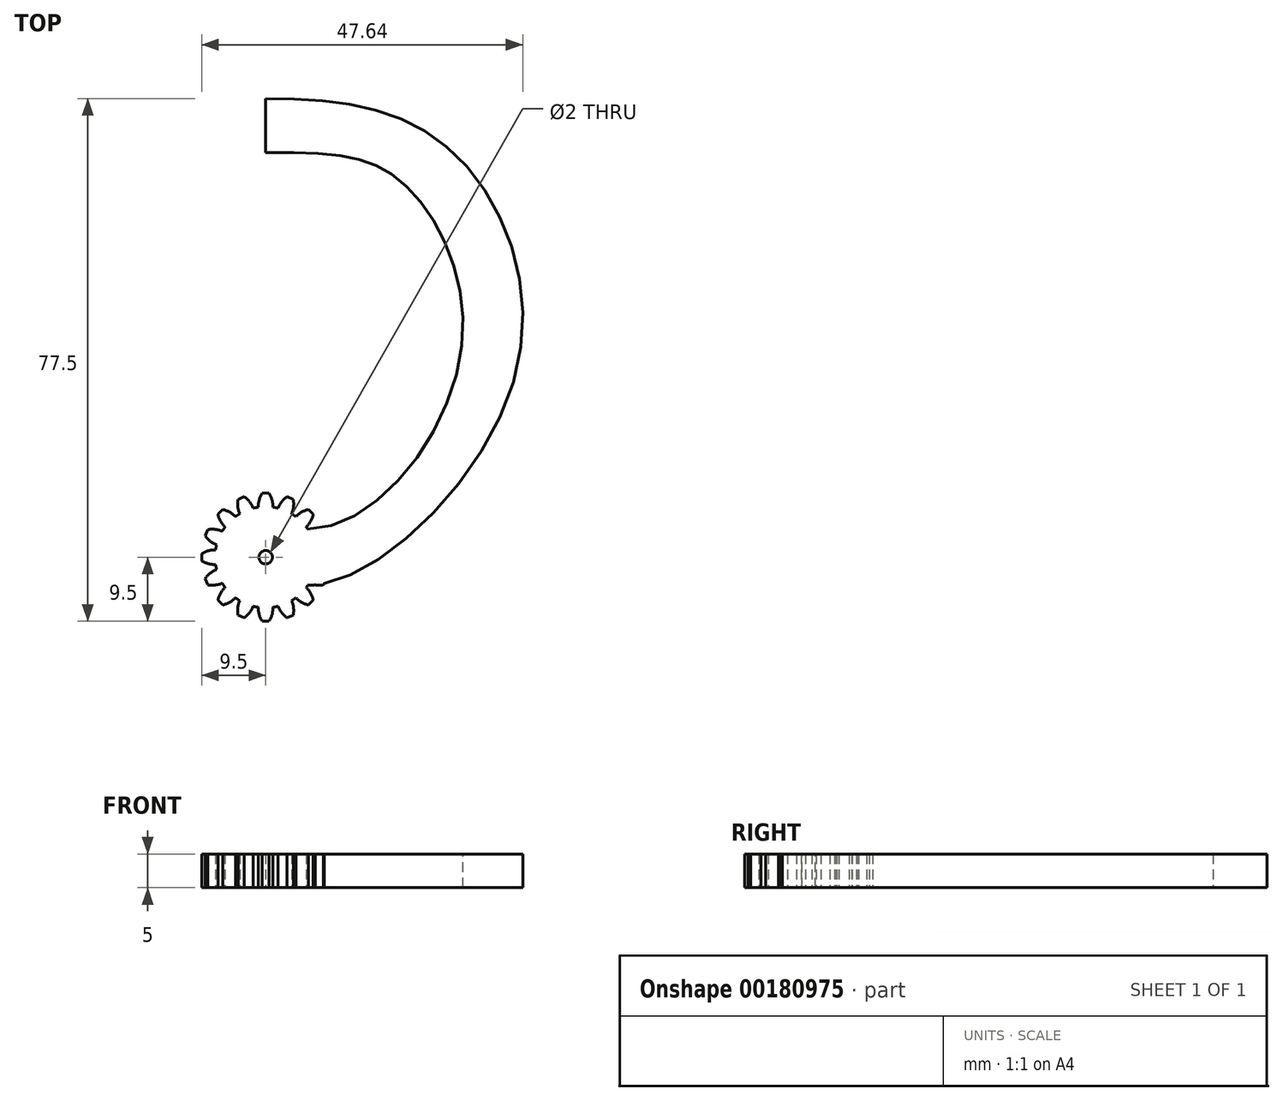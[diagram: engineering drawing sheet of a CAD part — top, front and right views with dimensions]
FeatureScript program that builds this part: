
annotation { "Feature Type Name" : "Feature", "Feature Type Description" : "" }
export const myFeature = defineFeature(function(context is Context, id is Id, definition is map)
    precondition{}
    {
        {
            var Q0;
            Q0=qCreatedBy(makeId("Top.planeOp"),FACE);
            var sketch = newSketch(context, id + "F0", { "sketchPlane" : qUnion([Q0])});
            skCircle(sketch, "E0", {"center": v(0, 0) * mm, "radius": 7.5 * mm});
            skLineSegment(sketch, "E1", {"start": v(0, 0) * mm, "end": v(0, 7.5) * mm, "construction": true});
            skLineSegment(sketch, "E2", {"start": v(0, 7.5) * mm, "end": v(0, 9.5) * mm});
            skLineSegment(sketch, "E3", {"start": v(0, 9.5) * mm, "end": v(-0.5, 9.5) * mm});
            skArc(sketch, "E4", {"start": v(-0.5, 9.5) * mm, "mid": v(-0.95, 8.5) * mm, "end": v(-1.09, 7.42) * mm});
            skLineSegment(sketch, "E5.MirrorCS", {"start": v(0, 9.5) * mm, "end": v(0.5, 9.5) * mm});
            skArc(sketch, "E6.MirrorCS", {"start": v(0.5, 9.5) * mm, "mid": v(0.95, 8.5) * mm, "end": v(1.09, 7.42) * mm});
            skArc(sketch, "E7.1.0", {"start": v(-4.1, 8.59) * mm, "mid": v(-4.13, 7.5) * mm, "end": v(-3.85, 6.44) * mm});
            skLineSegment(sketch, "E7.1.1", {"start": v(-3.64, 8.78) * mm, "end": v(-4.1, 8.59) * mm});
            skLineSegment(sketch, "E7.1.2", {"start": v(-3.64, 8.78) * mm, "end": v(-3.17, 8.97) * mm});
            skArc(sketch, "E7.1.3", {"start": v(-3.17, 8.97) * mm, "mid": v(-2.38, 8.22) * mm, "end": v(-1.83, 7.27) * mm});
            skArc(sketch, "E7.2.0", {"start": v(-7.07, 6.36) * mm, "mid": v(-6.69, 5.34) * mm, "end": v(-6.02, 4.48) * mm});
            skLineSegment(sketch, "E7.2.1", {"start": v(-6.72, 6.72) * mm, "end": v(-7.07, 6.36) * mm});
            skLineSegment(sketch, "E7.2.2", {"start": v(-6.72, 6.72) * mm, "end": v(-6.36, 7.07) * mm});
            skArc(sketch, "E7.2.3", {"start": v(-6.36, 7.07) * mm, "mid": v(-5.34, 6.69) * mm, "end": v(-4.48, 6.02) * mm});
            skArc(sketch, "E7.3.0", {"start": v(-8.97, 3.17) * mm, "mid": v(-8.22, 2.38) * mm, "end": v(-7.27, 1.83) * mm});
            skLineSegment(sketch, "E7.3.1", {"start": v(-8.78, 3.64) * mm, "end": v(-8.97, 3.17) * mm});
            skLineSegment(sketch, "E7.3.2", {"start": v(-8.78, 3.64) * mm, "end": v(-8.59, 4.1) * mm});
            skArc(sketch, "E7.3.3", {"start": v(-8.59, 4.1) * mm, "mid": v(-7.5, 4.13) * mm, "end": v(-6.44, 3.85) * mm});
            skArc(sketch, "E7.4.0", {"start": v(-9.5, -0.5) * mm, "mid": v(-8.5, -0.95) * mm, "end": v(-7.42, -1.09) * mm});
            skLineSegment(sketch, "E7.4.1", {"start": v(-9.5, 0) * mm, "end": v(-9.5, -0.5) * mm});
            skLineSegment(sketch, "E7.4.2", {"start": v(-9.5, 0) * mm, "end": v(-9.5, 0.5) * mm});
            skArc(sketch, "E7.4.3", {"start": v(-9.5, 0.5) * mm, "mid": v(-8.5, 0.95) * mm, "end": v(-7.42, 1.09) * mm});
            skArc(sketch, "E7.5.0", {"start": v(-8.59, -4.1) * mm, "mid": v(-7.5, -4.13) * mm, "end": v(-6.44, -3.85) * mm});
            skLineSegment(sketch, "E7.5.1", {"start": v(-8.78, -3.64) * mm, "end": v(-8.59, -4.1) * mm});
            skLineSegment(sketch, "E7.5.2", {"start": v(-8.78, -3.64) * mm, "end": v(-8.97, -3.17) * mm});
            skArc(sketch, "E7.5.3", {"start": v(-8.97, -3.17) * mm, "mid": v(-8.22, -2.38) * mm, "end": v(-7.27, -1.83) * mm});
            skArc(sketch, "E7.6.0", {"start": v(-6.36, -7.07) * mm, "mid": v(-5.34, -6.69) * mm, "end": v(-4.48, -6.02) * mm});
            skLineSegment(sketch, "E7.6.1", {"start": v(-6.72, -6.72) * mm, "end": v(-6.36, -7.07) * mm});
            skLineSegment(sketch, "E7.6.2", {"start": v(-6.72, -6.72) * mm, "end": v(-7.07, -6.36) * mm});
            skArc(sketch, "E7.6.3", {"start": v(-7.07, -6.36) * mm, "mid": v(-6.69, -5.34) * mm, "end": v(-6.02, -4.48) * mm});
            skArc(sketch, "E7.7.0", {"start": v(-3.17, -8.97) * mm, "mid": v(-2.38, -8.22) * mm, "end": v(-1.83, -7.27) * mm});
            skLineSegment(sketch, "E7.7.1", {"start": v(-3.64, -8.78) * mm, "end": v(-3.17, -8.97) * mm});
            skLineSegment(sketch, "E7.7.2", {"start": v(-3.64, -8.78) * mm, "end": v(-4.1, -8.59) * mm});
            skArc(sketch, "E7.7.3", {"start": v(-4.1, -8.59) * mm, "mid": v(-4.13, -7.5) * mm, "end": v(-3.85, -6.44) * mm});
            skArc(sketch, "E7.8.0", {"start": v(0.5, -9.5) * mm, "mid": v(0.95, -8.5) * mm, "end": v(1.09, -7.42) * mm});
            skLineSegment(sketch, "E7.8.1", {"start": v(0, -9.5) * mm, "end": v(0.5, -9.5) * mm});
            skLineSegment(sketch, "E7.8.2", {"start": v(0, -9.5) * mm, "end": v(-0.5, -9.5) * mm});
            skArc(sketch, "E7.8.3", {"start": v(-0.5, -9.5) * mm, "mid": v(-0.95, -8.5) * mm, "end": v(-1.09, -7.42) * mm});
            skArc(sketch, "E7.9.0", {"start": v(4.1, -8.59) * mm, "mid": v(4.13, -7.5) * mm, "end": v(3.85, -6.44) * mm});
            skLineSegment(sketch, "E7.9.1", {"start": v(3.64, -8.78) * mm, "end": v(4.1, -8.59) * mm});
            skLineSegment(sketch, "E7.9.2", {"start": v(3.64, -8.78) * mm, "end": v(3.17, -8.97) * mm});
            skArc(sketch, "E7.9.3", {"start": v(3.17, -8.97) * mm, "mid": v(2.38, -8.22) * mm, "end": v(1.83, -7.27) * mm});
            skArc(sketch, "E7.10.0", {"start": v(7.07, -6.36) * mm, "mid": v(6.69, -5.34) * mm, "end": v(6.02, -4.48) * mm});
            skLineSegment(sketch, "E7.10.1", {"start": v(6.72, -6.72) * mm, "end": v(7.07, -6.36) * mm});
            skLineSegment(sketch, "E7.10.2", {"start": v(6.72, -6.72) * mm, "end": v(6.36, -7.07) * mm});
            skArc(sketch, "E7.10.3", {"start": v(6.36, -7.07) * mm, "mid": v(5.34, -6.69) * mm, "end": v(4.48, -6.02) * mm});
            skArc(sketch, "E7.11.0", {"start": v(8.97, -3.17) * mm, "mid": v(8.22, -2.38) * mm, "end": v(7.27, -1.83) * mm});
            skLineSegment(sketch, "E7.11.1", {"start": v(8.78, -3.64) * mm, "end": v(8.97, -3.17) * mm});
            skLineSegment(sketch, "E7.11.2", {"start": v(8.78, -3.64) * mm, "end": v(8.59, -4.1) * mm});
            skArc(sketch, "E7.11.3", {"start": v(8.59, -4.1) * mm, "mid": v(7.5, -4.13) * mm, "end": v(6.44, -3.85) * mm});
            skArc(sketch, "E7.12.0", {"start": v(9.5, 0.5) * mm, "mid": v(8.5, 0.95) * mm, "end": v(7.42, 1.09) * mm});
            skLineSegment(sketch, "E7.12.1", {"start": v(9.5, 0) * mm, "end": v(9.5, 0.5) * mm});
            skLineSegment(sketch, "E7.12.2", {"start": v(9.5, 0) * mm, "end": v(9.5, -0.5) * mm});
            skArc(sketch, "E7.12.3", {"start": v(9.5, -0.5) * mm, "mid": v(8.5, -0.95) * mm, "end": v(7.42, -1.09) * mm});
            skArc(sketch, "E7.13.0", {"start": v(8.59, 4.1) * mm, "mid": v(7.5, 4.13) * mm, "end": v(6.44, 3.85) * mm});
            skLineSegment(sketch, "E7.13.1", {"start": v(8.78, 3.64) * mm, "end": v(8.59, 4.1) * mm});
            skLineSegment(sketch, "E7.13.2", {"start": v(8.78, 3.64) * mm, "end": v(8.97, 3.17) * mm});
            skArc(sketch, "E7.13.3", {"start": v(8.97, 3.17) * mm, "mid": v(8.22, 2.38) * mm, "end": v(7.27, 1.83) * mm});
            skArc(sketch, "E7.14.0", {"start": v(6.36, 7.07) * mm, "mid": v(5.34, 6.69) * mm, "end": v(4.48, 6.02) * mm});
            skLineSegment(sketch, "E7.14.1", {"start": v(6.72, 6.72) * mm, "end": v(6.36, 7.07) * mm});
            skLineSegment(sketch, "E7.14.2", {"start": v(6.72, 6.72) * mm, "end": v(7.07, 6.36) * mm});
            skArc(sketch, "E7.14.3", {"start": v(7.07, 6.36) * mm, "mid": v(6.69, 5.34) * mm, "end": v(6.02, 4.48) * mm});
            skArc(sketch, "E7.15.0", {"start": v(3.17, 8.97) * mm, "mid": v(2.38, 8.22) * mm, "end": v(1.83, 7.27) * mm});
            skLineSegment(sketch, "E7.15.1", {"start": v(3.64, 8.78) * mm, "end": v(3.17, 8.97) * mm});
            skLineSegment(sketch, "E7.15.2", {"start": v(3.64, 8.78) * mm, "end": v(4.1, 8.59) * mm});
            skArc(sketch, "E7.15.3", {"start": v(4.1, 8.59) * mm, "mid": v(4.13, 7.5) * mm, "end": v(3.85, 6.44) * mm});
            skSolve(sketch);
        }
        {
            var Q0;
            Q0=qSketchRegion(id+"F0",true);
            extrude(context, id + "F1", {"entities" : qUnion([Q0]), "depth" : 5 * mm});
        }
        {
            var Q0;
            Q0=makeQuery(id+"F1.opExtrude","CAP_FACE",FACE,{"disambiguationData":[OSD([sQuery(id+"F0.wireOp",EDGE,"E0"),sQuery(id+"F0.wireOp",EDGE,"E3"),sQuery(id+"F0.wireOp",EDGE,"E4"),sQuery(id+"F0.wireOp",EDGE,"E5.MirrorCS"),sQuery(id+"F0.wireOp",EDGE,"E6.MirrorCS"),sQuery(id+"F0.wireOp",EDGE,"E7.1.0"),sQuery(id+"F0.wireOp",EDGE,"E7.1.1"),sQuery(id+"F0.wireOp",EDGE,"E7.1.2"),sQuery(id+"F0.wireOp",EDGE,"E7.1.3"),sQuery(id+"F0.wireOp",EDGE,"E7.2.0"),sQuery(id+"F0.wireOp",EDGE,"E7.2.1"),sQuery(id+"F0.wireOp",EDGE,"E7.2.2"),sQuery(id+"F0.wireOp",EDGE,"E7.2.3"),sQuery(id+"F0.wireOp",EDGE,"E7.3.0"),sQuery(id+"F0.wireOp",EDGE,"E7.3.1"),sQuery(id+"F0.wireOp",EDGE,"E7.3.2"),sQuery(id+"F0.wireOp",EDGE,"E7.3.3"),sQuery(id+"F0.wireOp",EDGE,"E7.4.0"),sQuery(id+"F0.wireOp",EDGE,"E7.4.1"),sQuery(id+"F0.wireOp",EDGE,"E7.4.2"),sQuery(id+"F0.wireOp",EDGE,"E7.4.3"),sQuery(id+"F0.wireOp",EDGE,"E7.5.0"),sQuery(id+"F0.wireOp",EDGE,"E7.5.1"),sQuery(id+"F0.wireOp",EDGE,"E7.5.2"),sQuery(id+"F0.wireOp",EDGE,"E7.5.3"),sQuery(id+"F0.wireOp",EDGE,"E7.6.0"),sQuery(id+"F0.wireOp",EDGE,"E7.6.1"),sQuery(id+"F0.wireOp",EDGE,"E7.6.2"),sQuery(id+"F0.wireOp",EDGE,"E7.6.3"),sQuery(id+"F0.wireOp",EDGE,"E7.7.0"),sQuery(id+"F0.wireOp",EDGE,"E7.7.1"),sQuery(id+"F0.wireOp",EDGE,"E7.7.2"),sQuery(id+"F0.wireOp",EDGE,"E7.7.3"),sQuery(id+"F0.wireOp",EDGE,"E7.8.0"),sQuery(id+"F0.wireOp",EDGE,"E7.8.1"),sQuery(id+"F0.wireOp",EDGE,"E7.8.2"),sQuery(id+"F0.wireOp",EDGE,"E7.8.3"),sQuery(id+"F0.wireOp",EDGE,"E7.9.0"),sQuery(id+"F0.wireOp",EDGE,"E7.9.1"),sQuery(id+"F0.wireOp",EDGE,"E7.9.2"),sQuery(id+"F0.wireOp",EDGE,"E7.9.3"),sQuery(id+"F0.wireOp",EDGE,"E7.10.0"),sQuery(id+"F0.wireOp",EDGE,"E7.10.1"),sQuery(id+"F0.wireOp",EDGE,"E7.10.2"),sQuery(id+"F0.wireOp",EDGE,"E7.10.3"),sQuery(id+"F0.wireOp",EDGE,"E7.11.0"),sQuery(id+"F0.wireOp",EDGE,"E7.11.1"),sQuery(id+"F0.wireOp",EDGE,"E7.11.2"),sQuery(id+"F0.wireOp",EDGE,"E7.11.3"),sQuery(id+"F0.wireOp",EDGE,"E7.12.0"),sQuery(id+"F0.wireOp",EDGE,"E7.12.1"),sQuery(id+"F0.wireOp",EDGE,"E7.12.2"),sQuery(id+"F0.wireOp",EDGE,"E7.12.3"),sQuery(id+"F0.wireOp",EDGE,"E7.13.0"),sQuery(id+"F0.wireOp",EDGE,"E7.13.1"),sQuery(id+"F0.wireOp",EDGE,"E7.13.2"),sQuery(id+"F0.wireOp",EDGE,"E7.13.3"),sQuery(id+"F0.wireOp",EDGE,"E7.14.0"),sQuery(id+"F0.wireOp",EDGE,"E7.14.1"),sQuery(id+"F0.wireOp",EDGE,"E7.14.2"),sQuery(id+"F0.wireOp",EDGE,"E7.14.3"),sQuery(id+"F0.wireOp",EDGE,"E7.15.0"),sQuery(id+"F0.wireOp",EDGE,"E7.15.1"),sQuery(id+"F0.wireOp",EDGE,"E7.15.2"),sQuery(id+"F0.wireOp",EDGE,"E7.15.3")])],"isStart":false});
            var sketch = newSketch(context, id + "F2", { "sketchPlane" : qUnion([Q0])});
            skCircle(sketch, "E8", {"center": v(0, 0) * mm, "radius": 1 * mm});
            skSolve(sketch);
        }
        {
            var Q0;
            Q0=qSketchRegion(id+"F2",true);
            extrude(context, id + "F3", {"entities" : qUnion([Q0]), "operationType" : NewBodyOperationType.REMOVE, "endBound" : BoundingType.THROUGH_ALL, "oppositeDirection" : true, "depth" : 25 * mm});
        }
        {
            var Q0;
            Q0=qCreatedBy(makeId("Top.planeOp"),FACE);
            var sketch = newSketch(context, id + "F4", { "sketchPlane" : qUnion([Q0])});
            skLineSegment(sketch, "E9", {"start": v(0, 68) * mm, "end": v(0, 60) * mm});
            skFitSpline(sketch, "E10", {"points": [v(0, 60) * mm, v(20.23, 55.59) * mm, v(28.86, 29.66) * mm, v(6.24, 4.17) * mm], "startDerivative": vector(102.97, 0) * mm, "endDerivative": vector(-80.24, 0) * mm});
            skFitSpline(sketch, "E11", {"points": [v(0, 68) * mm, v(26.75, 60.96) * mm, v(36.79, 26.09) * mm, v(6.24, -4.17) * mm], "startDerivative": vector(101.77, 0) * mm, "endDerivative": vector(-81.62, 0) * mm});
            skLineSegment(sketch, "E12", {"start": v(6.24, 4.17) * mm, "end": v(6.24, -4.17) * mm});
            skSolve(sketch);
        }
        {
            var Q0;
            Q0 = qSketchRegion(id + "F4", true);
            var Q1;
            Q1=makeQuery(id+"F1.opExtrude","CAP_FACE",FACE,{"disambiguationData":[OSD([sQuery(id+"F0.wireOp",EDGE,"E0"),sQuery(id+"F0.wireOp",EDGE,"E3"),sQuery(id+"F0.wireOp",EDGE,"E4"),sQuery(id+"F0.wireOp",EDGE,"E5.MirrorCS"),sQuery(id+"F0.wireOp",EDGE,"E6.MirrorCS"),sQuery(id+"F0.wireOp",EDGE,"E7.1.0"),sQuery(id+"F0.wireOp",EDGE,"E7.1.1"),sQuery(id+"F0.wireOp",EDGE,"E7.1.2"),sQuery(id+"F0.wireOp",EDGE,"E7.1.3"),sQuery(id+"F0.wireOp",EDGE,"E7.2.0"),sQuery(id+"F0.wireOp",EDGE,"E7.2.1"),sQuery(id+"F0.wireOp",EDGE,"E7.2.2"),sQuery(id+"F0.wireOp",EDGE,"E7.2.3"),sQuery(id+"F0.wireOp",EDGE,"E7.3.0"),sQuery(id+"F0.wireOp",EDGE,"E7.3.1"),sQuery(id+"F0.wireOp",EDGE,"E7.3.2"),sQuery(id+"F0.wireOp",EDGE,"E7.3.3"),sQuery(id+"F0.wireOp",EDGE,"E7.4.0"),sQuery(id+"F0.wireOp",EDGE,"E7.4.1"),sQuery(id+"F0.wireOp",EDGE,"E7.4.2"),sQuery(id+"F0.wireOp",EDGE,"E7.4.3"),sQuery(id+"F0.wireOp",EDGE,"E7.5.0"),sQuery(id+"F0.wireOp",EDGE,"E7.5.1"),sQuery(id+"F0.wireOp",EDGE,"E7.5.2"),sQuery(id+"F0.wireOp",EDGE,"E7.5.3"),sQuery(id+"F0.wireOp",EDGE,"E7.6.0"),sQuery(id+"F0.wireOp",EDGE,"E7.6.1"),sQuery(id+"F0.wireOp",EDGE,"E7.6.2"),sQuery(id+"F0.wireOp",EDGE,"E7.6.3"),sQuery(id+"F0.wireOp",EDGE,"E7.7.0"),sQuery(id+"F0.wireOp",EDGE,"E7.7.1"),sQuery(id+"F0.wireOp",EDGE,"E7.7.2"),sQuery(id+"F0.wireOp",EDGE,"E7.7.3"),sQuery(id+"F0.wireOp",EDGE,"E7.8.0"),sQuery(id+"F0.wireOp",EDGE,"E7.8.1"),sQuery(id+"F0.wireOp",EDGE,"E7.8.2"),sQuery(id+"F0.wireOp",EDGE,"E7.8.3"),sQuery(id+"F0.wireOp",EDGE,"E7.9.0"),sQuery(id+"F0.wireOp",EDGE,"E7.9.1"),sQuery(id+"F0.wireOp",EDGE,"E7.9.2"),sQuery(id+"F0.wireOp",EDGE,"E7.9.3"),sQuery(id+"F0.wireOp",EDGE,"E7.10.0"),sQuery(id+"F0.wireOp",EDGE,"E7.10.1"),sQuery(id+"F0.wireOp",EDGE,"E7.10.2"),sQuery(id+"F0.wireOp",EDGE,"E7.10.3"),sQuery(id+"F0.wireOp",EDGE,"E7.11.0"),sQuery(id+"F0.wireOp",EDGE,"E7.11.1"),sQuery(id+"F0.wireOp",EDGE,"E7.11.2"),sQuery(id+"F0.wireOp",EDGE,"E7.11.3"),sQuery(id+"F0.wireOp",EDGE,"E7.12.0"),sQuery(id+"F0.wireOp",EDGE,"E7.12.1"),sQuery(id+"F0.wireOp",EDGE,"E7.12.2"),sQuery(id+"F0.wireOp",EDGE,"E7.12.3"),sQuery(id+"F0.wireOp",EDGE,"E7.13.0"),sQuery(id+"F0.wireOp",EDGE,"E7.13.1"),sQuery(id+"F0.wireOp",EDGE,"E7.13.2"),sQuery(id+"F0.wireOp",EDGE,"E7.13.3"),sQuery(id+"F0.wireOp",EDGE,"E7.14.0"),sQuery(id+"F0.wireOp",EDGE,"E7.14.1"),sQuery(id+"F0.wireOp",EDGE,"E7.14.2"),sQuery(id+"F0.wireOp",EDGE,"E7.14.3"),sQuery(id+"F0.wireOp",EDGE,"E7.15.0"),sQuery(id+"F0.wireOp",EDGE,"E7.15.1"),sQuery(id+"F0.wireOp",EDGE,"E7.15.2"),sQuery(id+"F0.wireOp",EDGE,"E7.15.3")])],"isStart":false});
            extrude(context, id + "F5", {"entities" : qUnion([Q0]), "operationType" : NewBodyOperationType.ADD, "endBound" : BoundingType.UP_TO_SURFACE, "endBoundEntityFace" : qUnion([Q1]), "depth" : 25 * mm});
        }
    });
